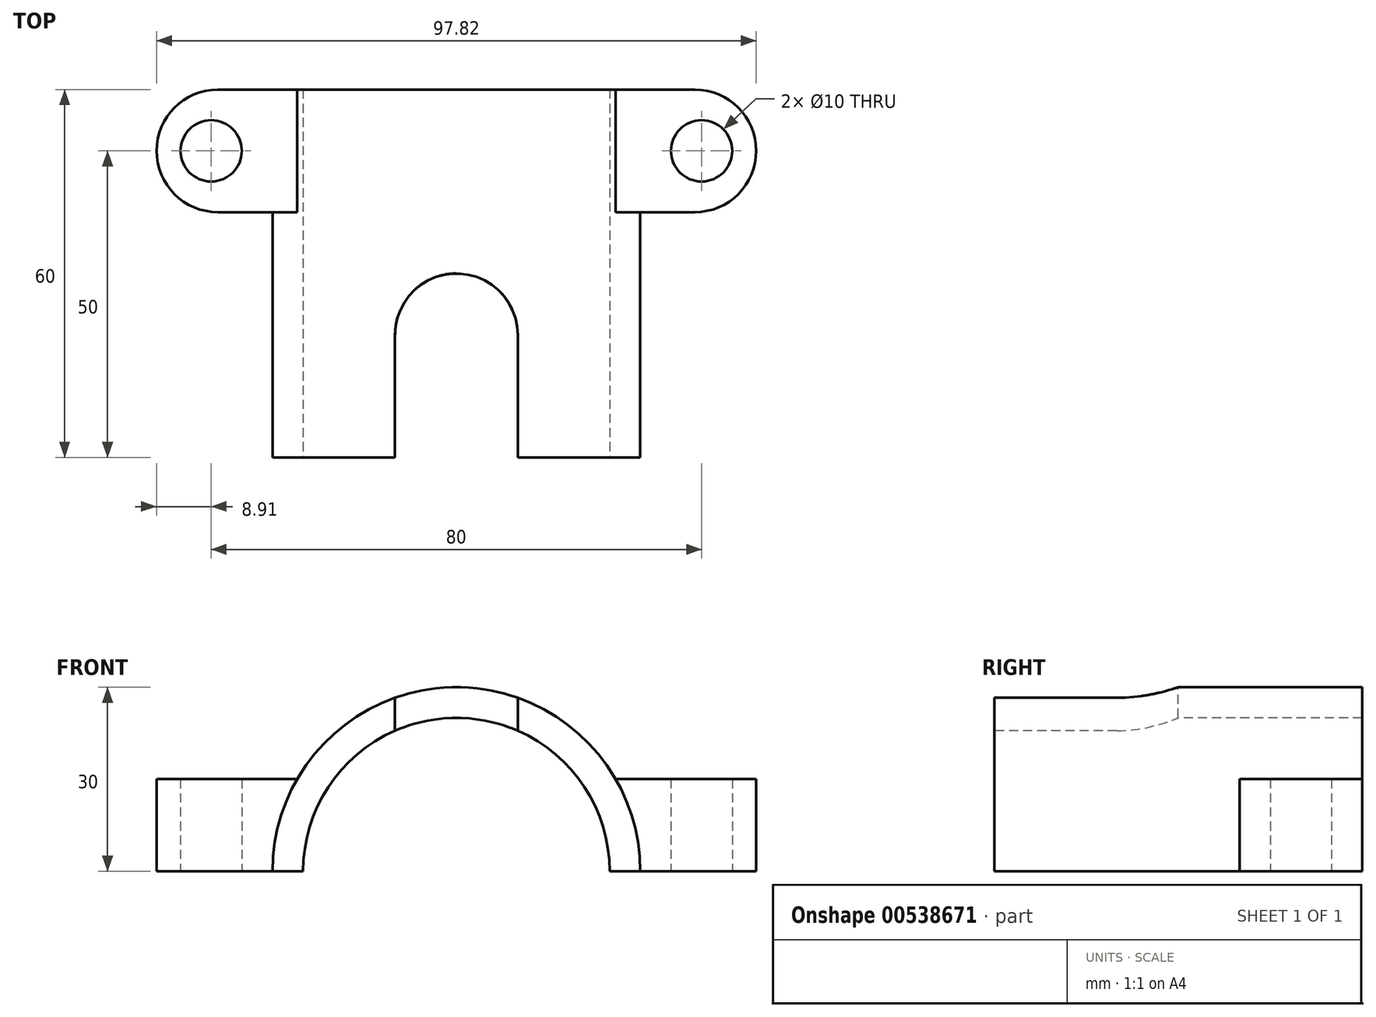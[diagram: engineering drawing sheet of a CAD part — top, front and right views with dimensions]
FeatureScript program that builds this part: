
annotation { "Feature Type Name" : "Feature", "Feature Type Description" : "" }
export const myFeature = defineFeature(function(context is Context, id is Id, definition is map)
    precondition{}
    {
        {
            assignVariable(context, id + "F0", {"name" : "A", "anyValue" : 15});
        }
        {
            var Q0;
            Q0=qCreatedBy(makeId("Front.planeOp"),FACE);
            var sketch = newSketch(context, id + "F1", { "sketchPlane" : qUnion([Q0])});
            skCircle(sketch, "E0", {"center": v(0, 0) * mm, "radius": 30 * mm});
            skSolve(sketch);
        }
        {
            var Q0;
            Q0 = qSketchRegion(id + "F1", true);
            extrude(context, id + "F2", {"entities" : qUnion([Q0]), "depth" : 60 * mm, "offsetDistance" : 25 * mm});
        }
        {
            var Q0;
            Q0=makeQuery(id+"F2.opExtrude","CAP_FACE",FACE,{"disambiguationData":[OSD([sQuery(id+"F1.wireOp",EDGE,"E0")])],"isStart":false});
            var sketch = newSketch(context, id + "F3", { "sketchPlane" : qUnion([Q0])});
            skArc(sketch, "E1", {"start": v(-30, 0) * mm, "mid": v(0, -30.09) * mm, "end": v(30, 0) * mm});
            skLineSegment(sketch, "E2", {"start": v(-30, 0) * mm, "end": v(30, 0) * mm});
            skSolve(sketch);
        }
        {
            var Q0;
            Q0 = qSketchRegion(id + "F3", true);
            extrude(context, id + "F4", {"entities" : qUnion([Q0]), "operationType" : NewBodyOperationType.REMOVE, "endBound" : BoundingType.UP_TO_NEXT, "oppositeDirection" : true, "depth" : 25 * mm, "offsetDistance" : 25 * mm});
        }
        {
            var Q0;
            Q0=qCreatedBy(makeId("Top.planeOp"),FACE);
            var sketch = newSketch(context, id + "F5", { "sketchPlane" : qUnion([Q0])});
            skLineSegment(sketch, "E3", {"start": v(-38.9, -10) * mm, "end": v(38.9, -10) * mm, "construction": true});
            skArc(sketch, "E4.0.startCap", {"start": v(-38.9, -20) * mm, "mid": v(-48.9, -10) * mm, "end": v(-38.9, 0) * mm});
            skArc(sketch, "E4.0.endCap", {"start": v(38.9, 0) * mm, "mid": v(48.9, -10) * mm, "end": v(38.9, -20) * mm});
            skLineSegment(sketch, "E4.0.left", {"start": v(-38.9, 0) * mm, "end": v(38.9, 0) * mm});
            skLineSegment(sketch, "E4.0.right", {"start": v(-38.9, -20) * mm, "end": v(38.9, -20) * mm});
            skSolve(sketch);
        }
        {
            var Q0;
            Q0 = qSketchRegion(id + "F5", true);
            extrude(context, id + "F6", {"entities" : qUnion([Q0]), "operationType" : NewBodyOperationType.ADD, "depth" : (getVariable(context, 'A')) * mm, "offsetDistance" : 25 * mm});
        }
        {
            var Q0;
            Q0=makeQuery(id+"F2.opExtrude","CAP_FACE",FACE,{"disambiguationData":[OSD([sQuery(id+"F1.wireOp",EDGE,"E0")])],"isStart":false});
            var sketch = newSketch(context, id + "F7", { "sketchPlane" : qUnion([Q0])});
            skArc(sketch, "E5", {"start": v(25, 0) * mm, "mid": v(0, 25) * mm, "end": v(-25, 0) * mm});
            skLineSegment(sketch, "E6", {"start": v(-25, 0) * mm, "end": v(25, 0) * mm});
            skSolve(sketch);
        }
        {
            var Q0;
            Q0 = qSketchRegion(id + "F7", true);
            extrude(context, id + "F8", {"entities" : qUnion([Q0]), "operationType" : NewBodyOperationType.REMOVE, "endBound" : BoundingType.UP_TO_NEXT, "oppositeDirection" : true, "depth" : 25 * mm, "offsetDistance" : 25 * mm});
        }
        {
            var Q0;
            Q0=qCreatedBy(makeId("Top.planeOp"),FACE);
            var sketch = newSketch(context, id + "F9", { "sketchPlane" : qUnion([Q0])});
            skLineSegment(sketch, "E7", {"start": v(0, 0) * mm, "end": v(-40, 0) * mm});
            skLineSegment(sketch, "E8", {"start": v(-40, 0) * mm, "end": v(-40, -10) * mm});
            skLineSegment(sketch, "E9", {"start": v(0, 0) * mm, "end": v(40, 0) * mm});
            skLineSegment(sketch, "E10", {"start": v(40, 0) * mm, "end": v(40, -10) * mm});
            skCircle(sketch, "E11", {"center": v(-40, -10) * mm, "radius": 5 * mm});
            skCircle(sketch, "E12", {"center": v(40, -10) * mm, "radius": 5 * mm});
            skSolve(sketch);
        }
        {
            var Q0;
            Q0 = qSketchRegion(id + "F9", true);
            extrude(context, id + "F10", {"entities" : qUnion([Q0]), "operationType" : NewBodyOperationType.REMOVE, "endBound" : BoundingType.THROUGH_ALL, "depth" : 25 * mm, "offsetDistance" : 25 * mm});
        }
        {
            var Q0;
            Q0=makeQuery(id+"F2.opExtrude","CAP_EDGE",EDGE,{"disambiguationData":[OSD([sQuery(id+"F1.wireOp",EDGE,"E0")])],"isStart":false});
            cPoint(context, id + "F11", {"entities" : qUnion([Q0]), "parameter" : 0.5});
        }
        {
            var Q0;
            Q0=qCreatedBy(makeId("Top.planeOp"),FACE);
            var Q1;
            Q1 = qCreatedBy(id + "F11" ,VERTEX);
            cPlane(context, id + "F12", {"entities" : qUnion([Q0, Q1]), "cplaneType" : CPlaneType.PLANE_POINT, "offset" : 25 * mm, "width" : 150 * mm, "height" : 150 * mm});
        }
        {
            var Q0;
            Q0=qCreatedBy(id+"F12.planeOp",FACE);
            var sketch = newSketch(context, id + "F13", { "sketchPlane" : qUnion([Q0])});
            skLineSegment(sketch, "E13", {"start": v(0, -30) * mm, "end": v(0, -60) * mm});
            skLineSegment(sketch, "E14", {"start": v(-10, -60) * mm, "end": v(-10, -40) * mm});
            skLineSegment(sketch, "E15", {"start": v(-10, -60) * mm, "end": v(0, -60) * mm});
            skArc(sketch, "E16", {"start": v(-10, -40) * mm, "mid": v(-7.07, -32.93) * mm, "end": v(0, -30) * mm});
            skArc(sketch, "E17.MirrorCS", {"start": v(10, -40) * mm, "mid": v(7.07, -32.93) * mm, "end": v(0, -30) * mm});
            skLineSegment(sketch, "E18.MirrorCS", {"start": v(10, -60) * mm, "end": v(10, -40) * mm});
            skLineSegment(sketch, "E19.MirrorCS", {"start": v(10, -60) * mm, "end": v(0, -60) * mm});
            skSolve(sketch);
        }
        {
            var Q0;
            Q0 = qSketchRegion(id + "F13", true);
            extrude(context, id + "F14", {"entities" : qUnion([Q0]), "operationType" : NewBodyOperationType.REMOVE, "endBound" : BoundingType.THROUGH_ALL, "oppositeDirection" : true, "depth" : 25 * mm, "offsetDistance" : 25 * mm});
        }
    });
